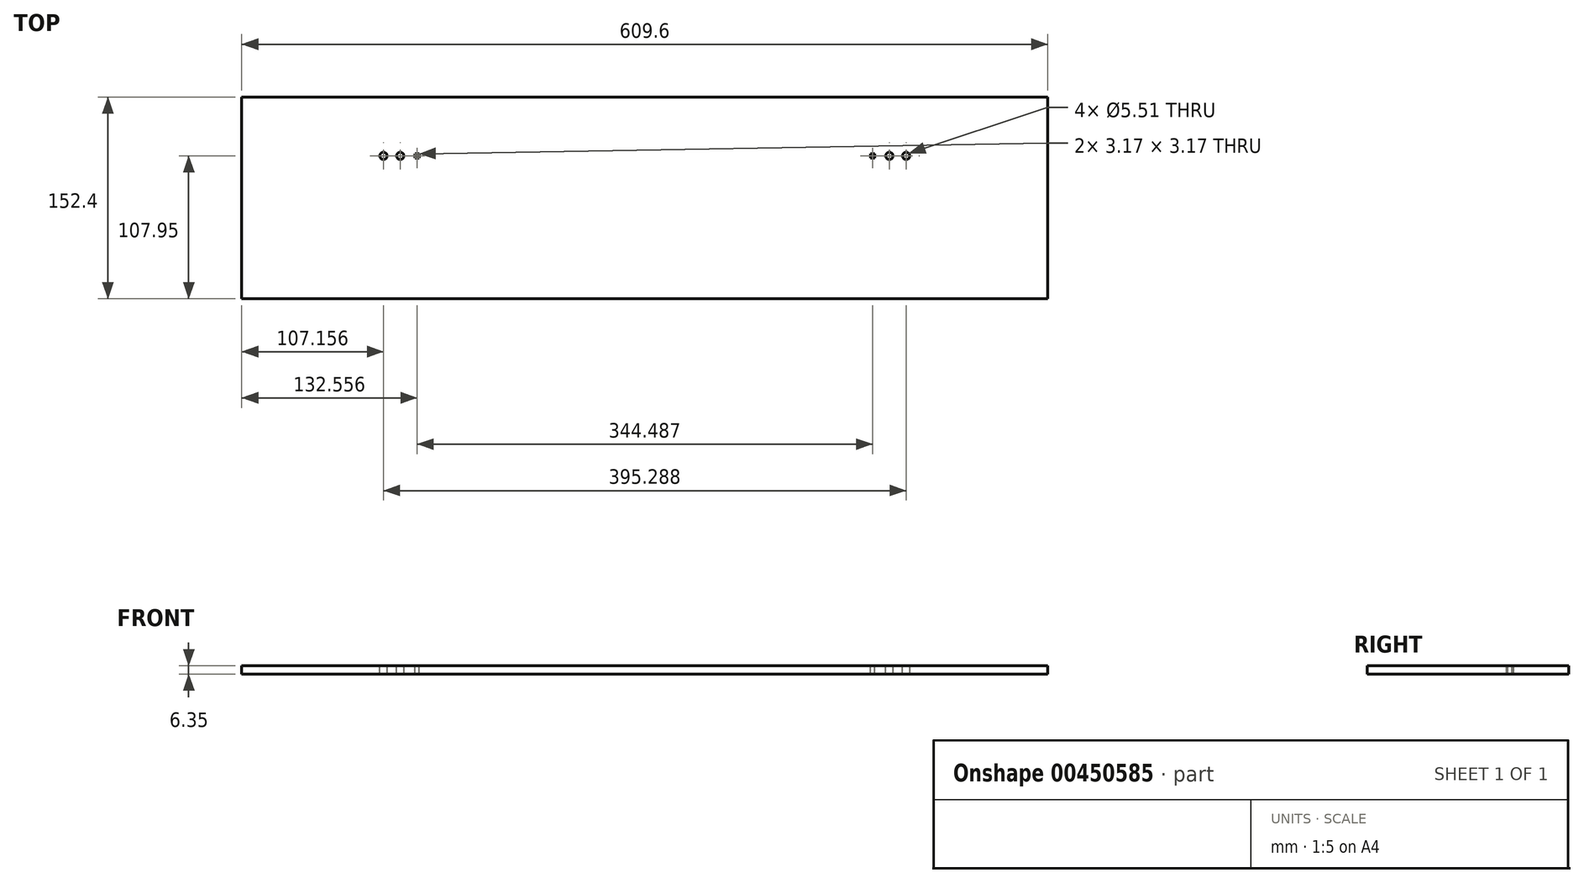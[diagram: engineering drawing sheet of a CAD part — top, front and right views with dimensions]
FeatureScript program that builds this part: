
annotation { "Feature Type Name" : "Feature", "Feature Type Description" : "" }
export const myFeature = defineFeature(function(context is Context, id is Id, definition is map)
    precondition{}
    {
        {
            var Q0;
            Q0=qCreatedBy(makeId("Top.planeOp"),FACE);
            var sketch = newSketch(context, id + "F0", { "sketchPlane" : qUnion([Q0])});
            skLineSegment(sketch, "E0.bottom", {"start": v(304.8, -76.2) * mm, "end": v(-304.8, -76.2) * mm});
            skLineSegment(sketch, "E0.top", {"start": v(304.8, 76.2) * mm, "end": v(-304.8, 76.2) * mm});
            skLineSegment(sketch, "E0.left", {"start": v(304.8, -76.2) * mm, "end": v(304.8, 76.2) * mm});
            skLineSegment(sketch, "E0.right", {"start": v(-304.8, -76.2) * mm, "end": v(-304.8, 76.2) * mm});
            skPoint(sketch, "E0.middle", {"position": v(0, 0) * mm});
            skSolve(sketch);
        }
        {
            var Q0;
            Q0 = qSketchRegion(id + "F0", true);
            extrude(context, id + "F1", {"entities" : qUnion([Q0]), "depth" : 6.35 * mm});
        }
        {
            var Q0;
            Q0=makeQuery(id+"F1.opExtrude","CAP_FACE",FACE,{"disambiguationData":[OSD([sQuery(id+"F0.wireOp",EDGE,"E0.bottom"),sQuery(id+"F0.wireOp",EDGE,"E0.top"),sQuery(id+"F0.wireOp",EDGE,"E0.left"),sQuery(id+"F0.wireOp",EDGE,"E0.right")])],"isStart":false});
            var sketch = newSketch(context, id + "F2", { "sketchPlane" : qUnion([Q0])});
            skLineSegment(sketch, "E1", {"start": v(-172.24, 0) * mm, "end": v(172.24, 0) * mm, "construction": true});
            skLineSegment(sketch, "E2", {"start": v(0, 41.2) * mm, "end": v(0, -69.97) * mm, "construction": true});
            skLineSegment(sketch, "E3", {"start": v(0, 31.75) * mm, "end": v(-153.42, 31.75) * mm, "construction": true});
            skCircle(sketch, "E4", {"center": v(-184.94, 31.75) * mm, "radius": 2.76 * mm});
            skCircle(sketch, "E5", {"center": v(-197.64, 31.75) * mm, "radius": 2.76 * mm});
            skCircle(sketch, "E6.MirrorC", {"center": v(184.94, 31.75) * mm, "radius": 2.76 * mm});
            skCircle(sketch, "E7.MirrorC", {"center": v(197.64, 31.75) * mm, "radius": 2.76 * mm});
            skLineSegment(sketch, "E8.bottom", {"start": v(-170.66, 30.16) * mm, "end": v(-173.83, 30.16) * mm});
            skLineSegment(sketch, "E8.top", {"start": v(-170.66, 33.34) * mm, "end": v(-173.83, 33.34) * mm});
            skLineSegment(sketch, "E8.left", {"start": v(-170.66, 30.16) * mm, "end": v(-170.66, 33.34) * mm});
            skLineSegment(sketch, "E8.right", {"start": v(-173.83, 30.16) * mm, "end": v(-173.83, 33.34) * mm});
            skPoint(sketch, "E8.middle", {"position": v(-172.24, 31.75) * mm});
            skLineSegment(sketch, "E9.MirrorCS", {"start": v(170.66, 30.16) * mm, "end": v(170.66, 33.34) * mm});
            skLineSegment(sketch, "E10.MirrorCS", {"start": v(170.66, 33.34) * mm, "end": v(173.83, 33.34) * mm});
            skLineSegment(sketch, "E11.MirrorCS", {"start": v(173.83, 30.16) * mm, "end": v(173.83, 33.34) * mm});
            skLineSegment(sketch, "E12.MirrorCS", {"start": v(170.66, 30.16) * mm, "end": v(173.83, 30.16) * mm});
            skSolve(sketch);
        }
        {
            var Q0;
            Q0 = qSketchRegion(id + "F2", true);
            extrude(context, id + "F3", {"entities" : qUnion([Q0]), "operationType" : NewBodyOperationType.REMOVE, "oppositeDirection" : true, "depth" : 6.35 * mm});
        }
    });
